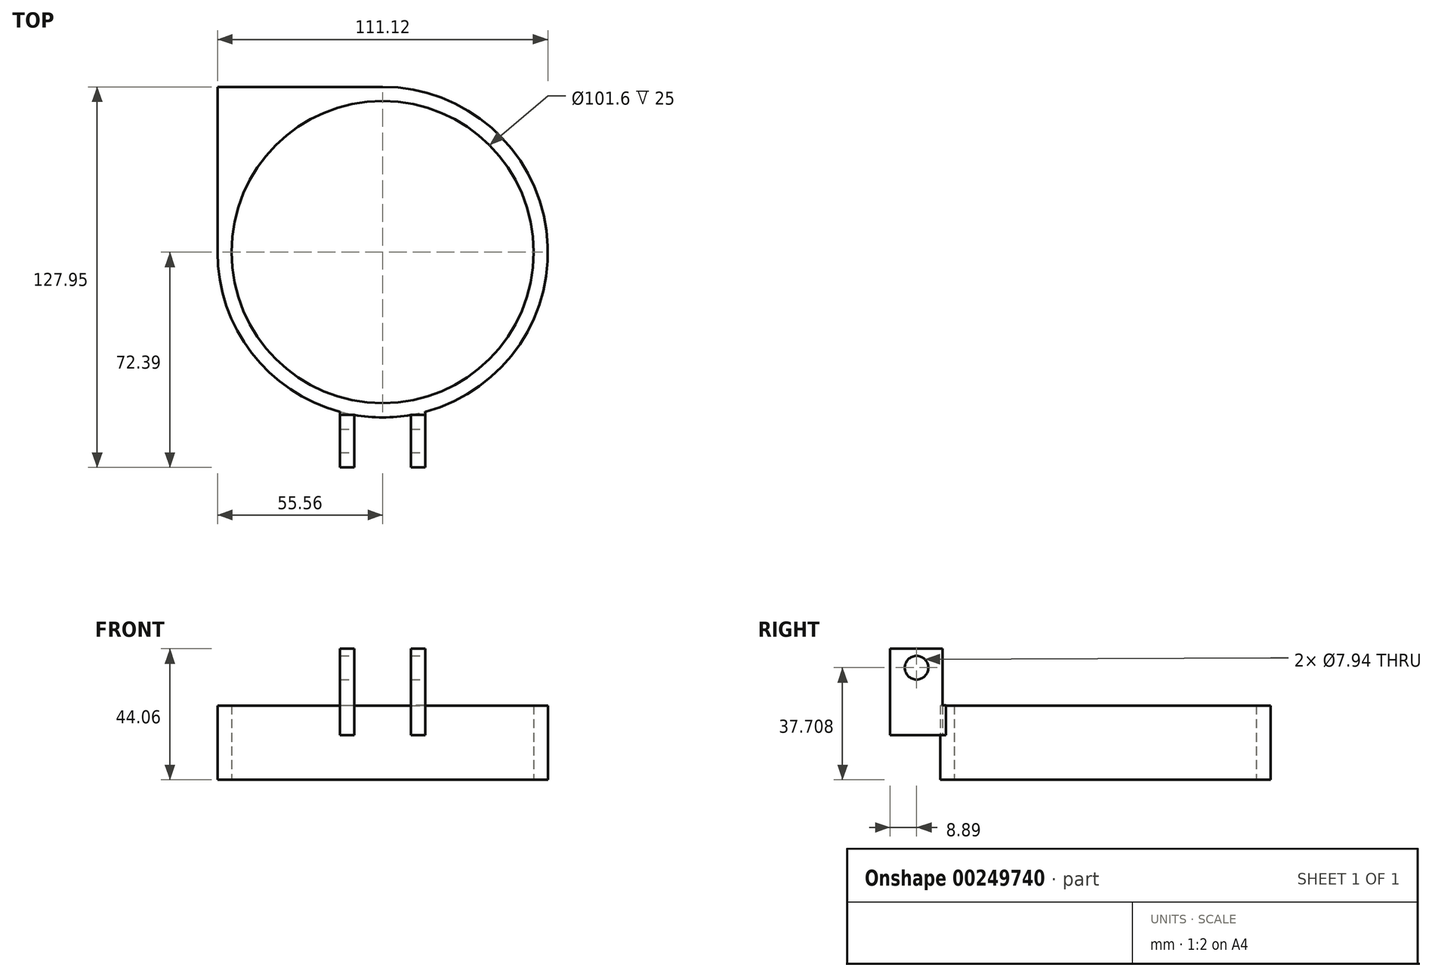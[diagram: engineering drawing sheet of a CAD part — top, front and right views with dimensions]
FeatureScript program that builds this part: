
annotation { "Feature Type Name" : "Feature", "Feature Type Description" : "" }
export const myFeature = defineFeature(function(context is Context, id is Id, definition is map)
    precondition{}
    {
        {
            var Q0;
            Q0=qCreatedBy(makeId("Top.planeOp"),FACE);
            var sketch = newSketch(context, id + "F0", { "sketchPlane" : qUnion([Q0])});
            skArc(sketch, "E0", {"start": v(-55.56, 0) * mm, "mid": v(39.29, -39.29) * mm, "end": v(0, 55.56) * mm});
            skCircle(sketch, "E1", {"center": v(0, 0) * mm, "radius": 50.8 * mm});
            skPoint(sketch, "E2", {"position": v(-55.56, 0) * mm});
            skPoint(sketch, "E3", {"position": v(0, 55.56) * mm});
            skLineSegment(sketch, "E4", {"start": v(-55.56, 0) * mm, "end": v(-55.56, 55.56) * mm});
            skLineSegment(sketch, "E5", {"start": v(0, 55.56) * mm, "end": v(-55.56, 55.56) * mm});
            skSolve(sketch);
        }
        {
            var Q0;
            Q0 = qSketchRegion(id + "F0", true);
            extrude(context, id + "F1", {"entities" : qUnion([Q0]), "depth" : 25 * mm});
        }
        {
            var Q0;
            Q0=qCreatedBy(makeId("Top.planeOp"),FACE);
            cPlane(context, id + "F2", {"entities" : qUnion([Q0]), "cplaneType" : CPlaneType.OFFSET, "offset" : 15 * mm, "width" : 150 * mm, "height" : 150 * mm});
        }
        {
            var Q0;
            Q0=qCreatedBy(id+"F2.planeOp",FACE);
            var sketch = newSketch(context, id + "F3", { "sketchPlane" : qUnion([Q0])});
            skLineSegment(sketch, "E6", {"start": v(0, 58.08) * mm, "end": v(0, -73.16) * mm, "construction": true});
            skPoint(sketch, "E7", {"position": v(0, -55.56) * mm});
            skPoint(sketch, "E8", {"position": v(0, -63.5) * mm});
            skLineSegment(sketch, "E9", {"start": v(0, -55.56) * mm, "end": v(9.55, -55.56) * mm, "construction": true});
            skLineSegment(sketch, "E10", {"start": v(9.55, -55.56) * mm, "end": v(-9.55, -55.56) * mm, "construction": true});
            skPoint(sketch, "E11", {"position": v(0, -50.8) * mm});
            skLineSegment(sketch, "E12.bottom", {"start": v(-9.55, -49.9) * mm, "end": v(-14.31, -49.9) * mm});
            skLineSegment(sketch, "E12.top", {"start": v(-9.55, -72.39) * mm, "end": v(-14.31, -72.39) * mm});
            skLineSegment(sketch, "E12.left", {"start": v(-9.55, -49.9) * mm, "end": v(-9.55, -72.39) * mm});
            skLineSegment(sketch, "E12.right", {"start": v(-14.31, -49.9) * mm, "end": v(-14.31, -72.39) * mm});
            skLineSegment(sketch, "E13.bottom", {"start": v(9.55, -49.9) * mm, "end": v(14.31, -49.9) * mm});
            skLineSegment(sketch, "E13.top", {"start": v(9.55, -72.39) * mm, "end": v(14.31, -72.39) * mm});
            skLineSegment(sketch, "E13.left", {"start": v(9.55, -49.9) * mm, "end": v(9.55, -72.39) * mm});
            skLineSegment(sketch, "E13.right", {"start": v(14.31, -49.9) * mm, "end": v(14.31, -72.39) * mm});
            skLineSegment(sketch, "E14", {"start": v(-9.55, -63.5) * mm, "end": v(9.55, -63.5) * mm, "construction": true});
            skSolve(sketch);
        }
        {
            var Q0;
            Q0 = qSketchRegion(id + "F3", true);
            extrude(context, id + "F4", {"entities" : qUnion([Q0]), "operationType" : NewBodyOperationType.ADD, "depth" : 10 * mm});
        }
        {
            var Q0;
            Q0=makeQuery(id+"F4.opExtrude","CAP_FACE",FACE,{"disambiguationData":[OSD([sQuery(id+"F3.wireOp",EDGE,"E13.bottom"),sQuery(id+"F3.wireOp",EDGE,"E13.top"),sQuery(id+"F3.wireOp",EDGE,"E13.left"),sQuery(id+"F3.wireOp",EDGE,"E13.right")])],"isStart":false});
            var sketch = newSketch(context, id + "F5", { "sketchPlane" : qUnion([Q0])});
            skLineSegment(sketch, "E15.bottom", {"start": v(14.31, -72.39) * mm, "end": v(9.55, -72.39) * mm});
            skLineSegment(sketch, "E15.top", {"start": v(14.31, -54.74) * mm, "end": v(9.55, -54.74) * mm});
            skLineSegment(sketch, "E15.left", {"start": v(14.31, -72.39) * mm, "end": v(14.31, -54.74) * mm});
            skLineSegment(sketch, "E15.right", {"start": v(9.55, -72.39) * mm, "end": v(9.55, -54.74) * mm});
            skLineSegment(sketch, "E16.bottom", {"start": v(-14.31, -72.39) * mm, "end": v(-9.55, -72.39) * mm});
            skLineSegment(sketch, "E16.top", {"start": v(-14.31, -54.74) * mm, "end": v(-9.55, -54.74) * mm});
            skLineSegment(sketch, "E16.left", {"start": v(-14.31, -72.39) * mm, "end": v(-14.31, -54.74) * mm});
            skLineSegment(sketch, "E16.right", {"start": v(-9.55, -72.39) * mm, "end": v(-9.55, -54.74) * mm});
            skSolve(sketch);
        }
        {
            var Q0;
            Q0 = qSketchRegion(id + "F5", true);
            extrude(context, id + "F6", {"entities" : qUnion([Q0]), "operationType" : NewBodyOperationType.ADD, "depth" : 19.05 * mm});
        }
        {
            var Q0;
            Q0=makeQuery(id+"F6.boolean.opBoolean","MERGE",FACE,{"derivedFrom":[makeQuery(id+"F4.opExtrude","SWEPT_FACE",FACE,{"disambiguationData":[OSD([sQuery(id+"F3.wireOp",EDGE,"E13.right")])]}),makeQuery(id+"F6.opExtrude","SWEPT_FACE",FACE,{"disambiguationData":[OSD([sQuery(id+"F5.wireOp",EDGE,"E15.left")])]})]});
            var sketch = newSketch(context, id + "F7", { "sketchPlane" : qUnion([Q0])});
            skLineSegment(sketch, "E17", {"start": v(-72.39, 37.7) * mm, "end": v(-54.74, 37.7) * mm, "construction": true});
            skPoint(sketch, "E18", {"position": v(-63.5, 37.7) * mm});
            skCircle(sketch, "E19", {"center": v(-63.5, 37.7) * mm, "radius": 3.97 * mm});
            skSolve(sketch);
        }
        {
            var Q0;
            Q0 = qSketchRegion(id + "F7", true);
            extrude(context, id + "F8", {"entities" : qUnion([Q0]), "operationType" : NewBodyOperationType.REMOVE, "endBound" : BoundingType.THROUGH_ALL, "oppositeDirection" : true, "depth" : 25.4 * mm});
        }
    });
